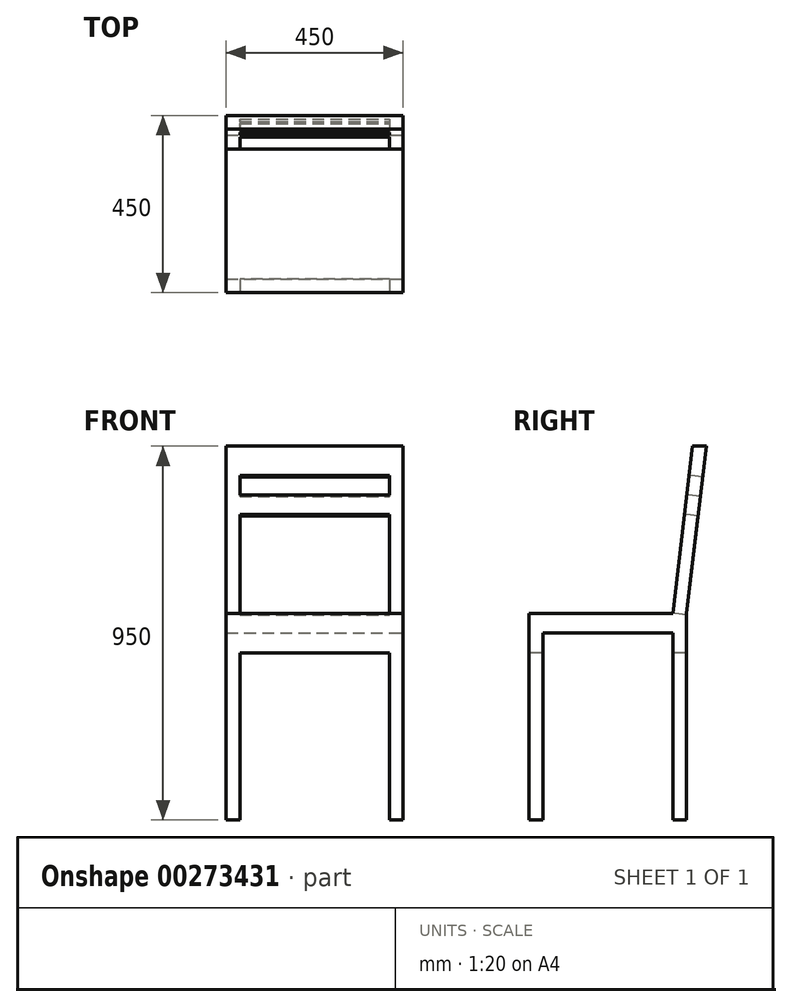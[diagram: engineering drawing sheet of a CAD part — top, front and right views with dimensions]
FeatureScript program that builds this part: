
annotation { "Feature Type Name" : "Feature", "Feature Type Description" : "" }
export const myFeature = defineFeature(function(context is Context, id is Id, definition is map)
    precondition{}
    {
        {
            var Q0;
            Q0=qCreatedBy(makeId("Top.planeOp"),FACE);
            var sketch = newSketch(context, id + "F0", { "sketchPlane" : qUnion([Q0])});
            skLineSegment(sketch, "E0.bottom", {"start": v(225, 225) * mm, "end": v(-225, 225) * mm});
            skLineSegment(sketch, "E0.top", {"start": v(225, -225) * mm, "end": v(-225, -225) * mm});
            skLineSegment(sketch, "E0.left", {"start": v(225, 225) * mm, "end": v(225, -225) * mm});
            skLineSegment(sketch, "E0.right", {"start": v(-225, 225) * mm, "end": v(-225, -225) * mm});
            skPoint(sketch, "E0.middle", {"position": v(0, 0) * mm});
            skSolve(sketch);
        }
        {
            var Q0;
            Q0=qSketchRegion(id+"F0",true);
            extrude(context, id + "F1", {"entities" : qUnion([Q0]), "depth" : 950 * mm});
        }
        {
            var Q0;
            Q0=makeQuery(id+"F1.opExtrude","SWEPT_FACE",FACE,{"disambiguationData":[OSD([sQuery(id+"F0.wireOp",EDGE,"E0.left")])]});
            var sketch = newSketch(context, id + "F2", { "sketchPlane" : qUnion([Q0])});
            skLineSegment(sketch, "E1.bottom", {"start": v(225, 475) * mm, "end": v(-225, 475) * mm});
            skLineSegment(sketch, "E1.top", {"start": v(225, 525) * mm, "end": v(-225, 525) * mm});
            skLineSegment(sketch, "E1.left", {"start": v(225, 475) * mm, "end": v(225, 525) * mm});
            skLineSegment(sketch, "E1.right", {"start": v(-225, 475) * mm, "end": v(-225, 525) * mm});
            skLineSegment(sketch, "E2.bottom", {"start": v(299.7, 504.41) * mm, "end": v(311, 504.41) * mm});
            skLineSegment(sketch, "E2.top", {"start": v(299.7, 511.95) * mm, "end": v(311, 511.95) * mm});
            skLineSegment(sketch, "E2.left", {"start": v(299.7, 504.41) * mm, "end": v(299.7, 511.95) * mm});
            skLineSegment(sketch, "E2.right", {"start": v(311, 504.41) * mm, "end": v(311, 511.95) * mm});
            skLineSegment(sketch, "E3", {"start": v(225, 950) * mm, "end": v(175, 525) * mm});
            skLineSegment(sketch, "E4", {"start": v(190, 950) * mm, "end": v(140, 525) * mm});
            skLineSegment(sketch, "E5", {"start": v(1132.44, 304.62) * mm, "end": v(1132.44, 325.37) * mm});
            skLineSegment(sketch, "E6", {"start": v(175, 525) * mm, "end": v(175, 0) * mm});
            skLineSegment(sketch, "E7", {"start": v(1006.16, 21.9) * mm, "end": v(1006.16, 0) * mm});
            skLineSegment(sketch, "E8", {"start": v(140, 525) * mm, "end": v(140, -13.92) * mm});
            skLineSegment(sketch, "E9.bottom", {"start": v(-190, 0) * mm, "end": v(-225, 0) * mm});
            skLineSegment(sketch, "E9.top", {"start": v(-190, 475) * mm, "end": v(-225, 475) * mm});
            skLineSegment(sketch, "E9.left", {"start": v(-190, 0) * mm, "end": v(-190, 475) * mm});
            skLineSegment(sketch, "E9.right", {"start": v(-225, 0) * mm, "end": v(-225, 475) * mm});
            skSolve(sketch);
        }
        {
            var Q0;
            Q0=makeQuery(id+"F2.imprint","IMPRINT",FACE,{"disambiguationData":[TD([[makeQuery(id+"F2.imprint","IMPRINT",EDGE,{"derivedFrom":sQuery(id+"F2.wireOp",EDGE,"E2.bottom")}),1.0]])]});
            var Q1;
            {var subQ4=sQuery(id+"F2.wireOp",EDGE,"E4");Q1=makeQuery(id+"F2.imprint","IMPRINT",FACE,{"disambiguationData":[TD([[makeQuery(id+"F2.imprint","IMPRINT",EDGE,{"derivedFrom":subQ4}),-1.0]])]});}
            var Q2;
            {var subQ0=sQuery(id+"F2.wireOp",EDGE,"E9.left");Q2=makeQuery(id+"F2.imprint","IMPRINT",FACE,{"disambiguationData":[TD([[makeQuery(id+"F2.imprint","IMPRINT",EDGE,{"derivedFrom":subQ0}),-1.0]])]});}
            var Q3;
            {var subQ1=sQuery(id+"F0.wireOp",EDGE,"E0.left");var subQ4=sQuery(id+"F2.wireOp",EDGE,"E6");var subQ6=makeQuery(id+"F1.opExtrude","CAP_EDGE",EDGE,{"disambiguationData":[OSD([subQ1])],"isStart":true});var subQ7=makeQuery(id+"F2.imprint","INTERSECT",VERTEX,{"derivedFrom":[subQ6,subQ4]});Q3=makeQuery(id+"F2.imprint","IMPRINT",FACE,{"disambiguationData":[TD([[makeQuery(id+"F2.imprint","IMPRINT",EDGE,{"disambiguationData":[TD([[subQ7,1.0]])],"derivedFrom":subQ4}),1.0]])]});}
            var Q4;
            {var subQ4=sQuery(id+"F2.wireOp",EDGE,"E3");Q4=makeQuery(id+"F2.imprint","IMPRINT",FACE,{"disambiguationData":[TD([[makeQuery(id+"F2.imprint","IMPRINT",EDGE,{"derivedFrom":subQ4}),1.0]])]});}
            var Q5;
            {var subQ0=sQuery(id+"F2.wireOp",EDGE,"E1.left");Q5=makeQuery(id+"F2.imprint","IMPRINT",FACE,{"disambiguationData":[TD([[makeQuery(id+"F2.imprint","IMPRINT",EDGE,{"derivedFrom":subQ0}),-1.0]])]});}
            extrude(context, id + "F3", {"entities" : qUnion([Q0, Q1, Q2, Q3, Q4, Q5]), "operationType" : NewBodyOperationType.REMOVE, "endBound" : BoundingType.THROUGH_ALL, "oppositeDirection" : true, "depth" : 25 * mm});
        }
        {
            var Q0;
            Q0=makeQuery(id+"F1.opExtrude","SWEPT_FACE",FACE,{"disambiguationData":[OSD([sQuery(id+"F0.wireOp",EDGE,"E0.top")])]});
            var sketch = newSketch(context, id + "F4", { "sketchPlane" : qUnion([Q0])});
            skLineSegment(sketch, "E10", {"start": v(-190, 0) * mm, "end": v(-190, 425) * mm});
            skLineSegment(sketch, "E11", {"start": v(-190, 425) * mm, "end": v(190, 425) * mm});
            skLineSegment(sketch, "E12", {"start": v(190, 425) * mm, "end": v(190, 0) * mm});
            skSolve(sketch);
        }
        {
            var Q0;
            Q0 = qSketchRegion(id + "F4", true);
            var Q1;
            {var subQ0=sQuery(id+"F4.wireOp",EDGE,"E10");Q1=makeQuery(id+"F4.imprint","IMPRINT",FACE,{"disambiguationData":[TD([[makeQuery(id+"F4.imprint","IMPRINT",EDGE,{"derivedFrom":subQ0}),-1.0]])]});}
            extrude(context, id + "F5", {"entities" : qUnion([Q0, Q1]), "operationType" : NewBodyOperationType.REMOVE, "endBound" : BoundingType.THROUGH_ALL, "oppositeDirection" : true, "depth" : 25 * mm});
        }
        {
            var Q0;
            Q0=makeQuery(id+"F3.boolean.opBoolean","COPY",FACE,{"derivedFrom":makeQuery(id+"F3.opExtrude","SWEPT_FACE",FACE,{"disambiguationData":[OSD([sQuery(id+"F2.wireOp",EDGE,"E4")])]})});
            var sketch = newSketch(context, id + "F6", { "sketchPlane" : qUnion([Q0])});
            skLineSegment(sketch, "E13", {"start": v(-190, 537.76) * mm, "end": v(-190, 890.7) * mm});
            skLineSegment(sketch, "E14", {"start": v(-190, 890.7) * mm, "end": v(190, 890.7) * mm});
            skLineSegment(sketch, "E15", {"start": v(190, 890.7) * mm, "end": v(190, 537.76) * mm});
            skPoint(sketch, "E16.startSnap0", {"position": v(-225, 751.73) * mm});
            skLineSegment(sketch, "E17", {"start": v(-190, 790.7) * mm, "end": v(190, 790.7) * mm});
            skLineSegment(sketch, "E18", {"start": v(-190, 840.7) * mm, "end": v(190, 840.7) * mm});
            skSolve(sketch);
        }
        {
            var Q0;
            {var subQ0=sQuery(id+"F6.wireOp",EDGE,"E14");Q0=makeQuery(id+"F6.imprint","IMPRINT",FACE,{"disambiguationData":[TD([[makeQuery(id+"F6.imprint","IMPRINT",EDGE,{"derivedFrom":subQ0}),-1.0]])]});}
            var Q1;
            {var subQ3=sQuery(id+"F6.wireOp",EDGE,"E17");Q1=makeQuery(id+"F6.imprint","IMPRINT",FACE,{"disambiguationData":[TD([[makeQuery(id+"F6.imprint","IMPRINT",EDGE,{"derivedFrom":subQ3}),-1.0]])]});}
            extrude(context, id + "F7", {"entities" : qUnion([Q0, Q1]), "operationType" : NewBodyOperationType.REMOVE, "endBound" : BoundingType.THROUGH_ALL, "oppositeDirection" : true, "depth" : 25 * mm});
        }
    });
